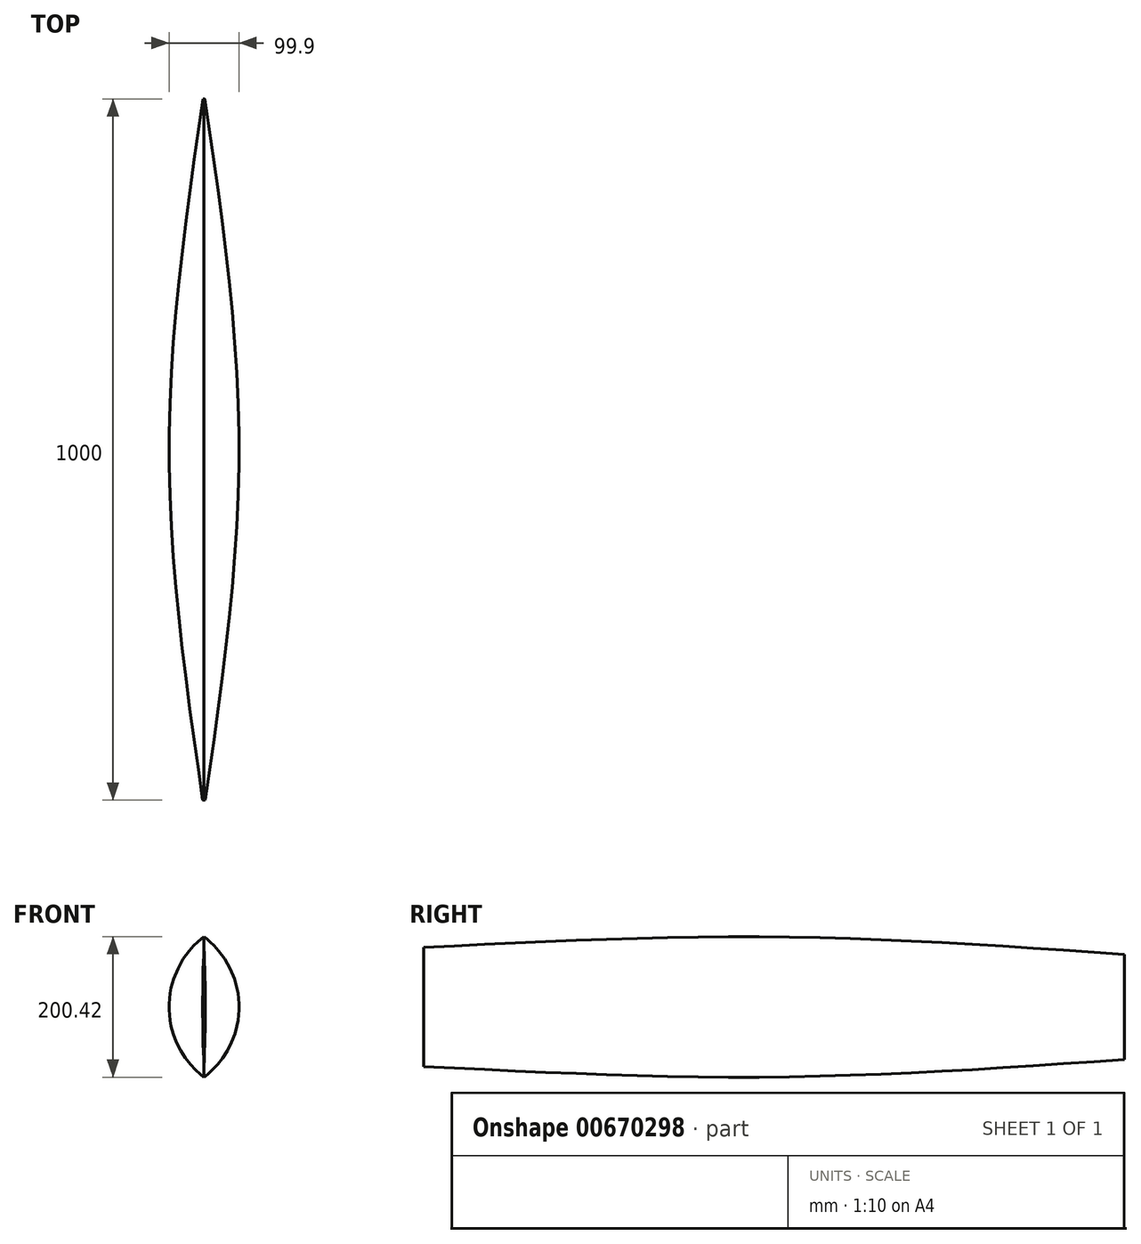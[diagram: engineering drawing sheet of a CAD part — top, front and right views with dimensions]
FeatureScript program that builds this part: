
annotation { "Feature Type Name" : "Feature", "Feature Type Description" : "" }
export const myFeature = defineFeature(function(context is Context, id is Id, definition is map)
    precondition{}
    {
        {
            var Q0;
            Q0=qCreatedBy(makeId("Front.planeOp"),FACE);
            cPlane(context, id + "F0", {"entities" : qUnion([Q0]), "cplaneType" : CPlaneType.OFFSET, "offset" : 500 * mm, "width" : 152.4 * mm, "height" : 152.4 * mm});
        }
        {
            var Q0;
            Q0=qCreatedBy(makeId("Front.planeOp"),FACE);
            cPlane(context, id + "F1", {"entities" : qUnion([Q0]), "cplaneType" : CPlaneType.OFFSET, "offset" : 500 * mm, "oppositeDirection" : true, "width" : 152.4 * mm, "height" : 152.4 * mm});
        }
        {
            var Q0;
            Q0=qCreatedBy(id+"F1.planeOp",FACE);
            var sketch = newSketch(context, id + "F2", { "sketchPlane" : qUnion([Q0])});
            skLineSegment(sketch, "E0.bottom", {"start": v(2.5, -75) * mm, "end": v(-2.5, -75) * mm});
            skLineSegment(sketch, "E0.top", {"start": v(2.5, 75) * mm, "end": v(-2.5, 75) * mm});
            skLineSegment(sketch, "E0.left", {"start": v(2.5, -75) * mm, "end": v(2.5, 75) * mm});
            skLineSegment(sketch, "E0.right", {"start": v(-2.5, -75) * mm, "end": v(-2.5, 75) * mm});
            skPoint(sketch, "E0.middle", {"position": v(0, 0) * mm});
            skArc(sketch, "E1", {"start": v(0, -75) * mm, "mid": v(1.43, 0) * mm, "end": v(0, 75) * mm});
            skArc(sketch, "E2", {"start": v(0, 75) * mm, "mid": v(-1.42, 0) * mm, "end": v(0, -75) * mm});
            skSolve(sketch);
        }
        {
            var Q0;
            Q0=qCreatedBy(id+"F0.planeOp",FACE);
            var sketch = newSketch(context, id + "F3", { "sketchPlane" : qUnion([Q0])});
            skLineSegment(sketch, "E3.bottom", {"start": v(2.5, -85) * mm, "end": v(-2.5, -85) * mm});
            skLineSegment(sketch, "E3.top", {"start": v(2.5, 85) * mm, "end": v(-2.5, 85) * mm});
            skLineSegment(sketch, "E3.left", {"start": v(2.5, -85) * mm, "end": v(2.5, 85) * mm});
            skLineSegment(sketch, "E3.right", {"start": v(-2.5, -85) * mm, "end": v(-2.5, 85) * mm});
            skPoint(sketch, "E3.middle", {"position": v(0, 0) * mm});
            skArc(sketch, "E4", {"start": v(0, -85) * mm, "mid": v(1.8, 0) * mm, "end": v(0, 85) * mm});
            skArc(sketch, "E5", {"start": v(0, 85) * mm, "mid": v(-1.8, 0) * mm, "end": v(0, -85) * mm});
            skSolve(sketch);
        }
        {
            var Q0;
            Q0=qCreatedBy(makeId("Front.planeOp"),FACE);
            var sketch = newSketch(context, id + "F4", { "sketchPlane" : qUnion([Q0])});
            skLineSegment(sketch, "E6.bottom", {"start": v(75, -100) * mm, "end": v(-75, -100) * mm});
            skLineSegment(sketch, "E6.top", {"start": v(75, 100) * mm, "end": v(-75, 100) * mm});
            skLineSegment(sketch, "E6.left", {"start": v(75, -100) * mm, "end": v(75, 100) * mm});
            skLineSegment(sketch, "E6.right", {"start": v(-75, -100) * mm, "end": v(-75, 100) * mm});
            skPoint(sketch, "E6.middle", {"position": v(0, 0) * mm});
            skArc(sketch, "E7", {"start": v(0, 100) * mm, "mid": v(-49.87, 0) * mm, "end": v(0, -100) * mm});
            skArc(sketch, "E8", {"start": v(0, -100) * mm, "mid": v(50.03, 0) * mm, "end": v(0, 100) * mm});
            skSolve(sketch);
        }
        {
            var Q0;
            Q0=makeQuery(id+"F2.imprint","IMPRINT",FACE,{"disambiguationData":[TD([[makeQuery(id+"F2.imprint","IMPRINT",EDGE,{"derivedFrom":sQuery(id+"F2.wireOp",EDGE,"E1")}),1.0]])]});
            var Q1;
            {var subQ4=sQuery(id+"F4.wireOp",EDGE,"E7");Q1=makeQuery(id+"F4.imprint","IMPRINT",FACE,{"disambiguationData":[TD([[makeQuery(id+"F4.imprint","IMPRINT",EDGE,{"derivedFrom":subQ4}),1.0]])]});}
            var Q2;
            Q2=makeQuery(id+"F3.imprint","IMPRINT",FACE,{"disambiguationData":[TD([[makeQuery(id+"F3.imprint","IMPRINT",EDGE,{"derivedFrom":sQuery(id+"F3.wireOp",EDGE,"E4")}),1.0]])]});
            loft(context, id + "F5", {"sheetProfilesArray" : [{ "sheetProfileEntities" : qUnion([Q0]) }, { "sheetProfileEntities" : qUnion([Q1]) }, { "sheetProfileEntities" : qUnion([Q2]) }]});
        }
    });
